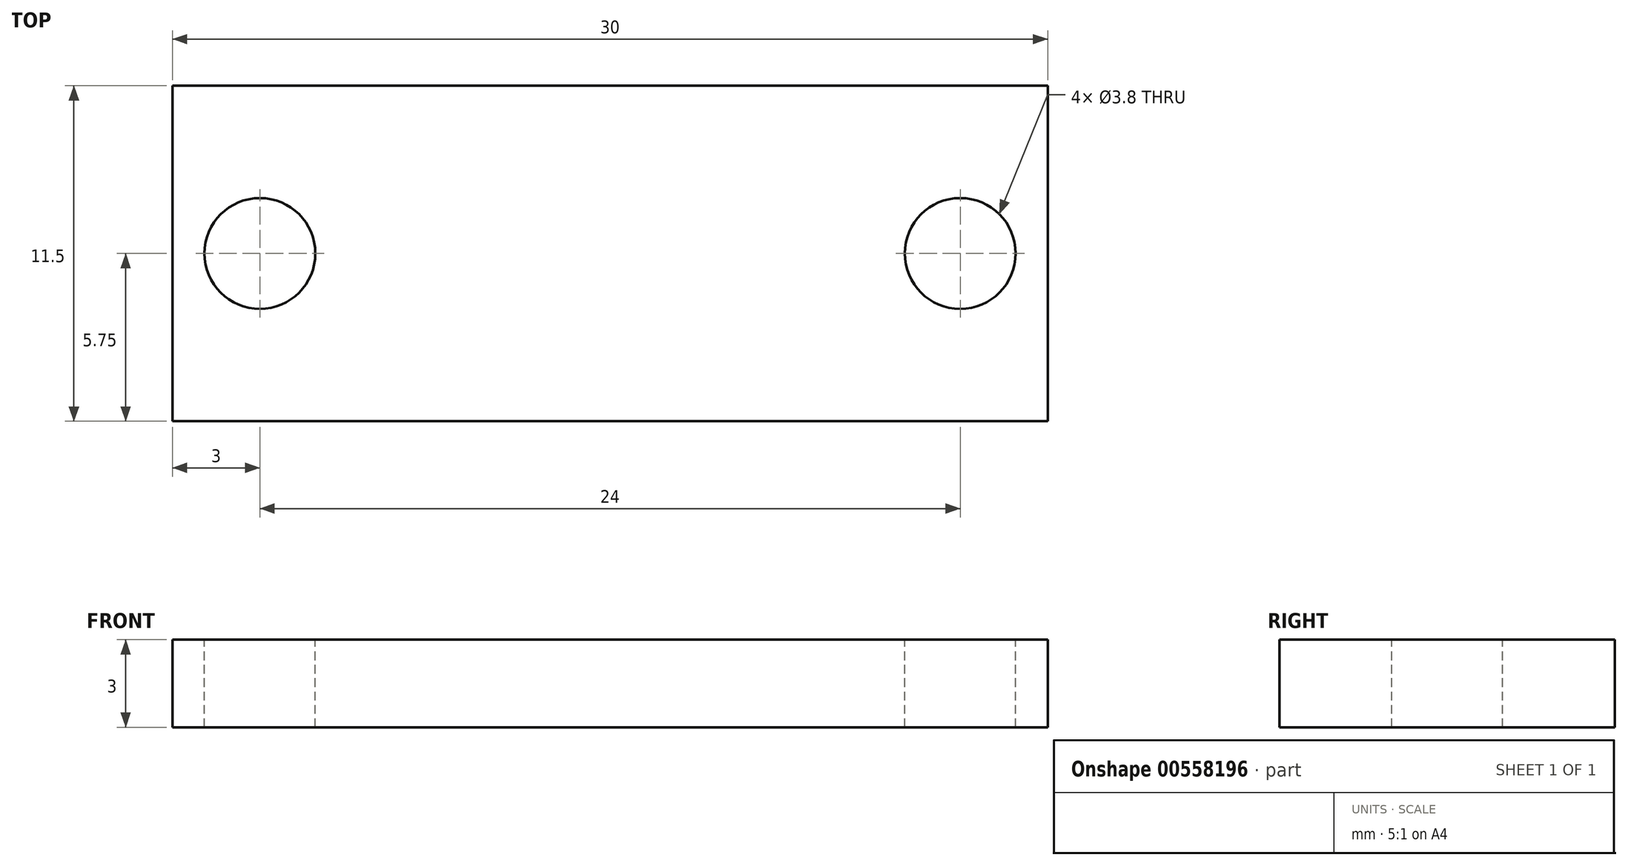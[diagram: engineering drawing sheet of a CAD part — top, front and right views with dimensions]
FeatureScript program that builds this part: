
annotation { "Feature Type Name" : "Feature", "Feature Type Description" : "" }
export const myFeature = defineFeature(function(context is Context, id is Id, definition is map)
    precondition{}
    {
        {
            var Q0;
            Q0=qCreatedBy(makeId("Top.planeOp"),FACE);
            var sketch = newSketch(context, id + "F0", { "sketchPlane" : qUnion([Q0])});
            skLineSegment(sketch, "E0.bottom", {"start": v(15, 5.75) * mm, "end": v(-15, 5.75) * mm});
            skLineSegment(sketch, "E0.top", {"start": v(15, -5.75) * mm, "end": v(-15, -5.75) * mm});
            skLineSegment(sketch, "E0.left", {"start": v(15, 5.75) * mm, "end": v(15, -5.75) * mm});
            skLineSegment(sketch, "E0.right", {"start": v(-15, 5.75) * mm, "end": v(-15, -5.75) * mm});
            skPoint(sketch, "E0.middle", {"position": v(0, 0) * mm});
            skSolve(sketch);
        }
        {
            var Q0;
            Q0 = qSketchRegion(id + "F0", true);
            extrude(context, id + "F1", {"entities" : qUnion([Q0]), "depth" : 3 * mm, "offsetDistance" : 25 * mm});
        }
        {
            var Q0;
            Q0=makeQuery(id+"F1.opExtrude","CAP_FACE",FACE,{"disambiguationData":[OSD([sQuery(id+"F0.wireOp",EDGE,"E0.bottom"),sQuery(id+"F0.wireOp",EDGE,"E0.top"),sQuery(id+"F0.wireOp",EDGE,"E0.left"),sQuery(id+"F0.wireOp",EDGE,"E0.right")])],"isStart":false});
            var sketch = newSketch(context, id + "F2", { "sketchPlane" : qUnion([Q0])});
            skPoint(sketch, "E1", {"position": v(-12, 0) * mm});
            skPoint(sketch, "E2.MirrorP", {"position": v(12, 0) * mm});
            skSolve(sketch);
        }
        {
            var Q0;
            Q0=sQuery(id+"F2.wireOp",VERTEX,"E1");
            var Q1;
            Q1=sQuery(id+"F2.wireOp",VERTEX,"E2.MirrorP");
            var Q2;
            Q2=makeQuery(id+"F1.opExtrude","SWEPT_BODY",BODY,{"disambiguationData":[OSD([sQuery(id+"F0.wireOp",EDGE,"E0.bottom"),sQuery(id+"F0.wireOp",EDGE,"E0.top"),sQuery(id+"F0.wireOp",EDGE,"E0.left"),sQuery(id+"F0.wireOp",EDGE,"E0.right")])]});
            hole(context, id + "F3", {"style" : HoleStyle.SIMPLE, "endStyle" : HoleEndStyle.THROUGH, "holeDiameter" : 3.8 * mm, "isTappedThrough" : true, "tappedDepth" : 12 * mm, "tapClearance" : 3, "locations" : qUnion([Q0, Q1]), "scope" : qUnion([Q2])});
        }
    });
